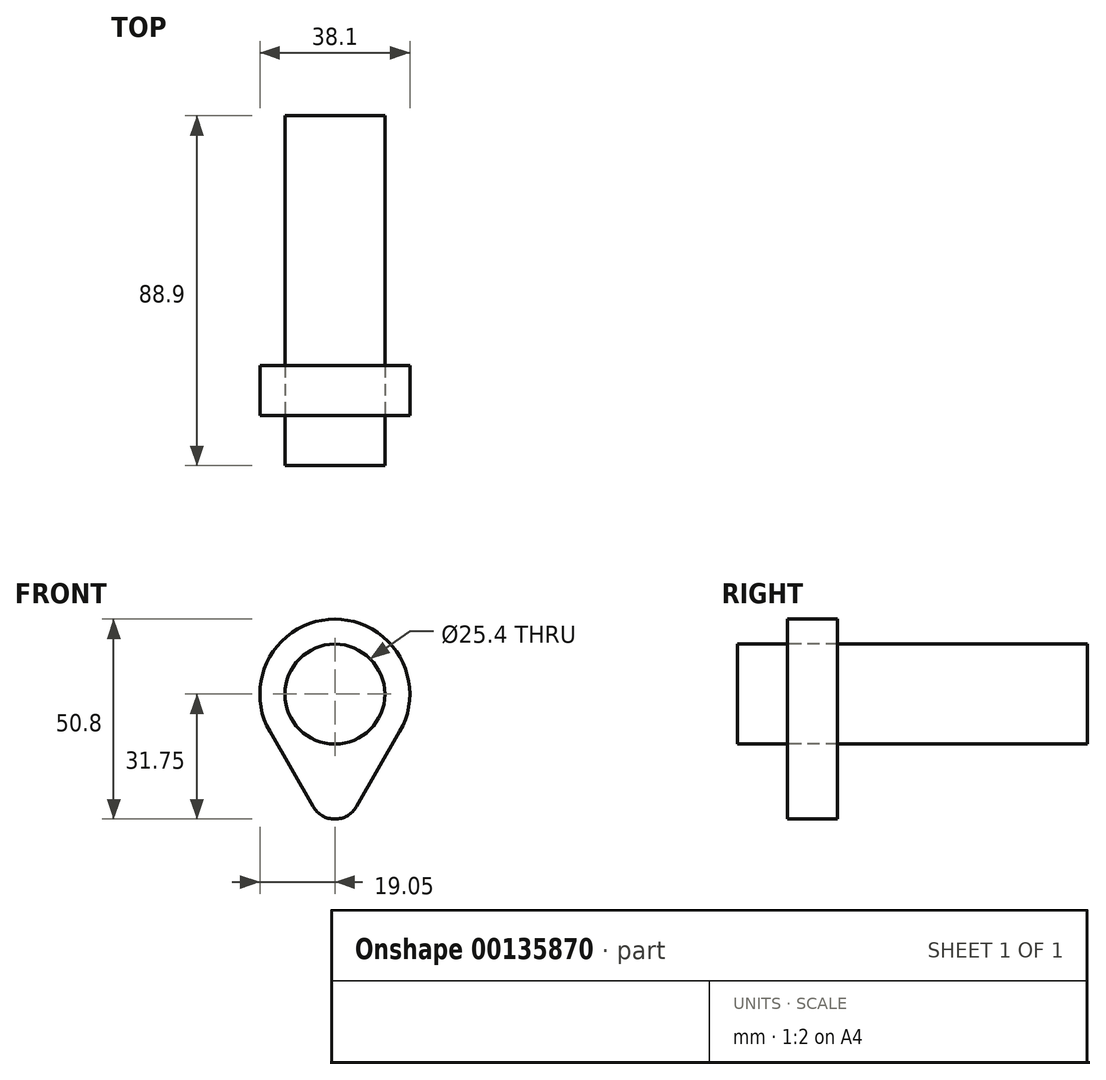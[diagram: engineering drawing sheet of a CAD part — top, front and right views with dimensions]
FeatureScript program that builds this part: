
annotation { "Feature Type Name" : "Feature", "Feature Type Description" : "" }
export const myFeature = defineFeature(function(context is Context, id is Id, definition is map)
    precondition{}
    {
        {
            var Q0;
            Q0=qCreatedBy(makeId("Front.planeOp"),FACE);
            var sketch = newSketch(context, id + "F0", { "sketchPlane" : qUnion([Q0])});
            skArc(sketch, "E0", {"start": v(16.5, -9.53) * mm, "mid": v(0, 19.05) * mm, "end": v(-16.5, -9.52) * mm});
            skLineSegment(sketch, "E1", {"start": v(0, 0) * mm, "end": v(0, -25.4) * mm});
            skArc(sketch, "E2", {"start": v(-5.5, -28.58) * mm, "mid": v(0, -31.75) * mm, "end": v(5.5, -28.57) * mm});
            skLineSegment(sketch, "E3", {"start": v(16.5, -9.53) * mm, "end": v(5.5, -28.57) * mm});
            skLineSegment(sketch, "E4", {"start": v(5.5, -28.58) * mm, "end": v(16.5, -9.52) * mm});
            skLineSegment(sketch, "E5", {"start": v(-16.5, -9.53) * mm, "end": v(-5.5, -28.58) * mm});
            skCircle(sketch, "E6", {"center": v(0, 0) * mm, "radius": 12.7 * mm});
            skSolve(sketch);
        }
        {
            var Q0;
            Q0=makeQuery(id+"F0.imprint","IMPRINT",FACE,{"disambiguationData":[TD([[makeQuery(id+"F0.imprint","IMPRINT",EDGE,{"derivedFrom":sQuery(id+"F0.wireOp",EDGE,"E0")}),1.0]])]});
            extrude(context, id + "F1", {"entities" : qUnion([Q0]), "depth" : 12.7 * mm});
        }
        {
            var Q0;
            Q0=qCreatedBy(makeId("Front.planeOp"),FACE);
            cPlane(context, id + "F2", {"entities" : qUnion([Q0]), "cplaneType" : CPlaneType.OFFSET, "offset" : 25.4 * mm, "width" : 152.4 * mm, "height" : 152.4 * mm});
        }
        {
            var Q0;
            Q0=qCreatedBy(id+"F2.planeOp",FACE);
            var sketch = newSketch(context, id + "F3", { "sketchPlane" : qUnion([Q0])});
            skCircle(sketch, "E7", {"center": v(0, 0) * mm, "radius": 12.7 * mm});
            skSolve(sketch);
        }
        {
            var Q0;
            Q0 = qSketchRegion(id + "F3", true);
            extrude(context, id + "F4", {"entities" : qUnion([Q0]), "oppositeDirection" : true, "depth" : 88.9 * mm});
        }
    });
